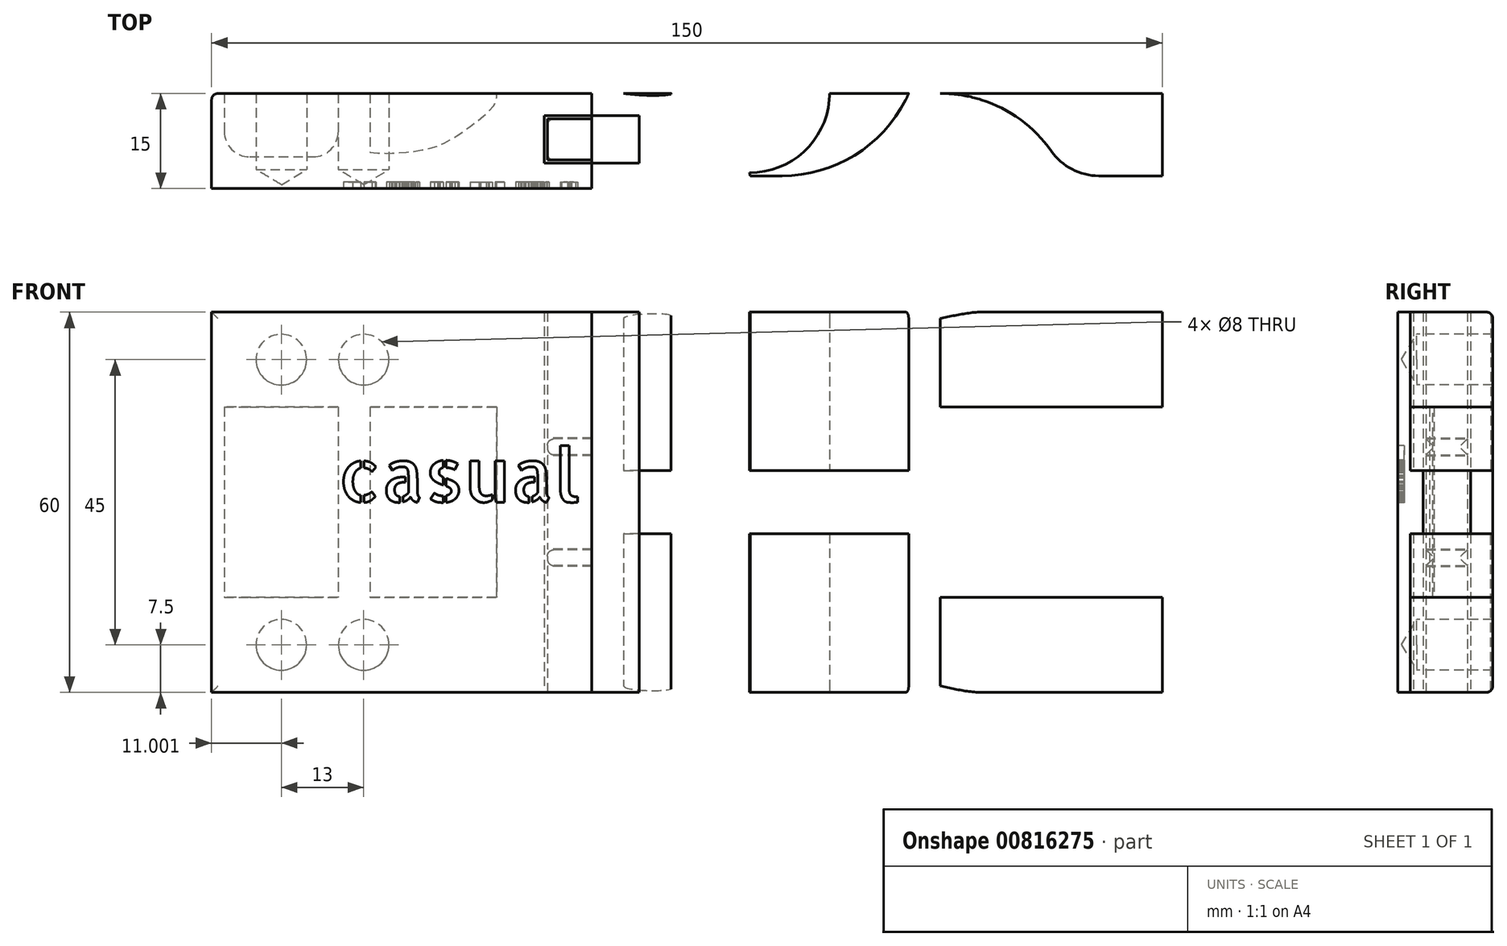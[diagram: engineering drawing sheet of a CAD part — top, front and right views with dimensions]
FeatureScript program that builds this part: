
annotation { "Feature Type Name" : "Feature", "Feature Type Description" : "" }
export const myFeature = defineFeature(function(context is Context, id is Id, definition is map)
    precondition{}
    {
        {
            var Q0;
            Q0=qCreatedBy(makeId("Top.planeOp"),FACE);
            var sketch = newSketch(context, id + "F0", { "sketchPlane" : qUnion([Q0])});
            skLineSegment(sketch, "E0.bottom", {"start": v(91.44, -7.74) * mm, "end": v(-58.56, -7.74) * mm});
            skLineSegment(sketch, "E0.top", {"start": v(91.44, 7.26) * mm, "end": v(-58.56, 7.26) * mm});
            skLineSegment(sketch, "E0.left", {"start": v(91.44, -7.74) * mm, "end": v(91.44, 7.26) * mm});
            skLineSegment(sketch, "E0.right", {"start": v(-58.56, -7.74) * mm, "end": v(-58.56, 7.26) * mm});
            skLineSegment(sketch, "E1", {"start": v(91.44, -5.74) * mm, "end": v(81.44, -5.74) * mm});
            skArc(sketch, "E2", {"start": v(81.44, -5.74) * mm, "mid": v(77.21, -4.7) * mm, "end": v(73.94, -1.84) * mm});
            skArc(sketch, "E3", {"start": v(73.94, -1.84) * mm, "mid": v(66.3, 4.85) * mm, "end": v(56.44, 7.26) * mm});
            skLineSegment(sketch, "E4", {"start": v(26.44, -5.74) * mm, "end": v(31.44, -5.74) * mm});
            skArc(sketch, "E5", {"start": v(31.44, -5.74) * mm, "mid": v(43.37, -2.2) * mm, "end": v(51.44, 7.26) * mm});
            skLineSegment(sketch, "E6", {"start": v(-58.56, -5.74) * mm, "end": v(106.76, -5.74) * mm, "construction": true});
            skFitSpline(sketch, "E7", {"points": [v(26.44, -5.74) * mm, v(25.26, -0.18) * mm, v(21.4, 5.71) * mm, v(6.44, 7.26) * mm], "startDerivative": vector(-4.01, 21.25) * mm, "endDerivative": vector(-55.89, 0) * mm});
            skLineSegment(sketch, "E8.bottom", {"start": v(-56.56, 7.26) * mm, "end": v(-38.56, 7.26) * mm});
            skLineSegment(sketch, "E8.top", {"start": v(-52.56, -2.74) * mm, "end": v(-42.56, -2.74) * mm});
            skLineSegment(sketch, "E8.left", {"start": v(-56.56, 7.26) * mm, "end": v(-56.56, 1.26) * mm});
            skLineSegment(sketch, "E8.right", {"start": v(-38.56, 7.26) * mm, "end": v(-38.56, 1.26) * mm});
            skLineSegment(sketch, "E9", {"start": v(-33.56, 7.26) * mm, "end": v(-33.56, -1.98) * mm});
            skFitSpline(sketch, "E10", {"points": [v(-33.56, -1.98) * mm, v(-29.23, -1.98) * mm, v(-23.5, -0.86) * mm, v(-18.2, 2.03) * mm, v(-13.56, 7.26) * mm], "startDerivative": vector(19.96, -2.18) * mm, "endDerivative": vector(3.98, 19.09) * mm});
            skPoint(sketch, "E11.visualSharp", {"position": v(-56.56, -2.74) * mm});
            skArc(sketch, "E11.filletArc", {"start": v(-56.56, 1.26) * mm, "mid": v(-55.39, -1.56) * mm, "end": v(-52.56, -2.74) * mm});
            skPoint(sketch, "E12.visualSharp", {"position": v(-38.56, -2.74) * mm});
            skArc(sketch, "E12.filletArc", {"start": v(-42.56, -2.74) * mm, "mid": v(-39.73, -1.56) * mm, "end": v(-38.56, 1.26) * mm});
            skCircle(sketch, "E13", {"center": v(26.44, 7.26) * mm, "radius": 12.5 * mm});
            skSolve(sketch);
        }
        {
            var Q0;
            Q0=qCreatedBy(makeId("Top.planeOp"),FACE);
            var sketch = newSketch(context, id + "F1", { "sketchPlane" : qUnion([Q0])});
            skFitSpline(sketch, "E14.0", {"points": [v(-33.56, -1.98) * mm, v(-32.12, -2.14) * mm, v(-29.23, -2.11) * mm, v(-23.2, -1.12) * mm, v(-18.34, 1.63) * mm, v(-13.92, 5.51) * mm, v(-13.56, 7.26) * mm]});
            skLineSegment(sketch, "E14.1", {"start": v(-33.56, 7.26) * mm, "end": v(-33.56, -1.98) * mm});
            skLineSegment(sketch, "E14.2", {"start": v(-38.56, 7.26) * mm, "end": v(-38.56, 1.26) * mm});
            skArc(sketch, "E14.3", {"start": v(-42.56, -2.74) * mm, "mid": v(-39.73, -1.56) * mm, "end": v(-38.56, 1.26) * mm});
            skLineSegment(sketch, "E14.4", {"start": v(-52.56, -2.74) * mm, "end": v(-42.56, -2.74) * mm});
            skArc(sketch, "E14.5", {"start": v(-56.56, 1.26) * mm, "mid": v(-55.39, -1.56) * mm, "end": v(-52.56, -2.74) * mm});
            skLineSegment(sketch, "E14.6", {"start": v(-56.56, 7.26) * mm, "end": v(-56.56, 1.26) * mm});
            skLineSegment(sketch, "E14.8", {"start": v(-58.56, -7.74) * mm, "end": v(-58.56, 7.26) * mm});
            skLineSegment(sketch, "E15", {"start": v(-58.56, -7.74) * mm, "end": v(1.44, -7.74) * mm});
            skLineSegment(sketch, "E16", {"start": v(1.44, -7.74) * mm, "end": v(1.44, 7.26) * mm});
            skLineSegment(sketch, "E17", {"start": v(1.44, 7.26) * mm, "end": v(-58.56, 7.26) * mm});
            skLineSegment(sketch, "E18.bottom", {"start": v(8.94, -3.75) * mm, "end": v(-6.06, -3.75) * mm});
            skLineSegment(sketch, "E18.top", {"start": v(8.94, 3.75) * mm, "end": v(-6.06, 3.75) * mm});
            skLineSegment(sketch, "E18.left", {"start": v(8.94, -3.75) * mm, "end": v(8.94, 3.75) * mm});
            skLineSegment(sketch, "E18.right", {"start": v(-6.06, -3.75) * mm, "end": v(-6.06, 3.75) * mm});
            skPoint(sketch, "E18.middle", {"position": v(1.44, 0) * mm});
            skFitSpline(sketch, "E19.0", {"points": [v(26.44, -5.74) * mm, v(26.08, -3.84) * mm, v(25.69, -0.2) * mm, v(21.45, 7.91) * mm, v(14.55, 7.26) * mm, v(6.44, 7.26) * mm]});
            skArc(sketch, "E19.1", {"start": v(31.44, -5.74) * mm, "mid": v(43.37, -2.2) * mm, "end": v(51.44, 7.26) * mm});
            skLineSegment(sketch, "E19.2", {"start": v(26.44, -5.74) * mm, "end": v(31.44, -5.74) * mm});
            skArc(sketch, "E19.3", {"start": v(73.94, -1.84) * mm, "mid": v(66.3, 4.85) * mm, "end": v(56.44, 7.26) * mm});
            skArc(sketch, "E19.4", {"start": v(81.44, -5.74) * mm, "mid": v(77.21, -4.7) * mm, "end": v(73.94, -1.84) * mm});
            skLineSegment(sketch, "E19.5", {"start": v(91.44, -5.74) * mm, "end": v(81.44, -5.74) * mm});
            skCircle(sketch, "E19.7", {"center": v(26.44, 7.26) * mm, "radius": 12.5 * mm});
            skLineSegment(sketch, "E20.bottom", {"start": v(1.44, 7.26) * mm, "end": v(91.44, 7.26) * mm});
            skLineSegment(sketch, "E20.top", {"start": v(1.44, -7.74) * mm, "end": v(91.44, -7.74) * mm});
            skLineSegment(sketch, "E20.left", {"start": v(1.44, 7.26) * mm, "end": v(1.44, -7.74) * mm});
            skLineSegment(sketch, "E20.right", {"start": v(91.44, 7.26) * mm, "end": v(91.44, -7.74) * mm});
            skLineSegment(sketch, "E21.0", {"start": v(8.94, 3.25) * mm, "end": v(-5.56, 3.25) * mm});
            skLineSegment(sketch, "E21.1", {"start": v(-5.56, -3.25) * mm, "end": v(-5.56, 3.25) * mm});
            skLineSegment(sketch, "E21.2", {"start": v(8.94, -3.25) * mm, "end": v(-5.56, -3.25) * mm});
            skSolve(sketch);
        }
        {
            var Q0;
            {var subQ5=sQuery(id+"F1.wireOp",EDGE,"E18.right");Q0=makeQuery(id+"F1.imprint","IMPRINT",FACE,{"disambiguationData":[TD([[makeQuery(id+"F1.imprint","IMPRINT",EDGE,{"derivedFrom":subQ5}),-1.0]])]});}
            var Q1;
            {var subQ6=sQuery(id+"F1.wireOp",EDGE,"E14.0");Q1=makeQuery(id+"F1.imprint","IMPRINT",FACE,{"disambiguationData":[TD([[makeQuery(id+"F1.imprint","IMPRINT",EDGE,{"derivedFrom":subQ6}),-1.0]])]});}
            var Q2;
            {var subQ0=sQuery(id+"F1.wireOp",EDGE,"E14.0");Q2=makeQuery(id+"F1.imprint","IMPRINT",FACE,{"disambiguationData":[TD([[makeQuery(id+"F1.imprint","IMPRINT",EDGE,{"derivedFrom":subQ0}),1.0]])]});}
            var Q3;
            {var subQ1=sQuery(id+"F1.wireOp",EDGE,"E14.2");Q3=makeQuery(id+"F1.imprint","IMPRINT",FACE,{"disambiguationData":[TD([[makeQuery(id+"F1.imprint","IMPRINT",EDGE,{"derivedFrom":subQ1}),-1.0]])]});}
            var Q4;
            {var subQ5=sQuery(id+"F1.wireOp",EDGE,"E21.1");Q4=makeQuery(id+"F1.imprint","IMPRINT",FACE,{"disambiguationData":[TD([[makeQuery(id+"F1.imprint","IMPRINT",EDGE,{"derivedFrom":subQ5}),-1.0]])]});}
            extrude(context, id + "F2", {"entities" : qUnion([Q0, Q1, Q2, Q3, Q4]), "depth" : 60 * mm, "offsetDistance" : 25 * mm, "symmetric" : true});
        }
        {
            var Q0;
            {var subQ1=sQuery(id+"F1.wireOp",EDGE,"E14.2");Q0=makeQuery(id+"F1.imprint","IMPRINT",FACE,{"disambiguationData":[TD([[makeQuery(id+"F1.imprint","IMPRINT",EDGE,{"derivedFrom":subQ1}),-1.0]])]});}
            var Q1;
            {var subQ0=sQuery(id+"F1.wireOp",EDGE,"E14.0");Q1=makeQuery(id+"F1.imprint","IMPRINT",FACE,{"disambiguationData":[TD([[makeQuery(id+"F1.imprint","IMPRINT",EDGE,{"derivedFrom":subQ0}),1.0]])]});}
            extrude(context, id + "F3", {"entities" : qUnion([Q0, Q1]), "operationType" : NewBodyOperationType.REMOVE, "depth" : 30 * mm, "offsetDistance" : 25 * mm, "symmetric" : true});
        }
        {
            var Q0;
            {var subQ5=sQuery(id+"F1.wireOp",EDGE,"E18.right");Q0=makeQuery(id+"F1.imprint","IMPRINT",FACE,{"disambiguationData":[TD([[makeQuery(id+"F1.imprint","IMPRINT",EDGE,{"derivedFrom":subQ5}),-1.0]])]});}
            var Q1;
            {var subQ5=sQuery(id+"F1.wireOp",EDGE,"E21.1");Q1=makeQuery(id+"F1.imprint","IMPRINT",FACE,{"disambiguationData":[TD([[makeQuery(id+"F1.imprint","IMPRINT",EDGE,{"derivedFrom":subQ5}),-1.0]])]});}
            extrude(context, id + "F4", {"entities" : qUnion([Q0, Q1]), "operationType" : NewBodyOperationType.REMOVE, "depth" : 20.25 * mm, "offsetDistance" : 25 * mm, "symmetric" : true});
        }
        {
            var Q0;
            {var subQ4=sQuery(id+"F1.wireOp",EDGE,"E18.left");Q0=makeQuery(id+"F1.imprint","IMPRINT",FACE,{"disambiguationData":[TD([[makeQuery(id+"F1.imprint","IMPRINT",EDGE,{"derivedFrom":subQ4}),-1.0]])]});}
            var Q1;
            {var subQ0=sQuery(id+"F1.wireOp",EDGE,"E18.left");Q1=makeQuery(id+"F1.imprint","IMPRINT",FACE,{"disambiguationData":[TD([[makeQuery(id+"F1.imprint","IMPRINT",EDGE,{"derivedFrom":subQ0}),1.0]])]});}
            extrude(context, id + "F5", {"entities" : qUnion([Q0, Q1]), "depth" : 60 * mm, "offsetDistance" : 25 * mm, "symmetric" : true});
        }
        {
            var Q0;
            {var subQ0=sQuery(id+"F1.wireOp",EDGE,"E19.7");var subQ1=sQuery(id+"F1.wireOp",EDGE,"E19.0");var subQ2=makeQuery(id+"F1.imprint","INTERSECT",VERTEX,{"disambiguationData":[OD(1.0)],"derivedFrom":[subQ1,subQ0]});Q0=makeQuery(id+"F1.imprint","IMPRINT",FACE,{"disambiguationData":[TD([[makeQuery(id+"F1.imprint","IMPRINT",EDGE,{"disambiguationData":[TD([[subQ2,-1.0]])],"derivedFrom":subQ1}),-1.0]])]});}
            var Q1;
            {var subQ0=sQuery(id+"F1.wireOp",EDGE,"E19.7");var subQ1=sQuery(id+"F1.wireOp",EDGE,"E19.0");var subQ2=makeQuery(id+"F1.imprint","INTERSECT",VERTEX,{"disambiguationData":[OD(1.0)],"derivedFrom":[subQ1,subQ0]});Q1=makeQuery(id+"F1.imprint","IMPRINT",FACE,{"disambiguationData":[TD([[makeQuery(id+"F1.imprint","IMPRINT",EDGE,{"disambiguationData":[TD([[subQ2,-1.0]])],"derivedFrom":subQ1}),1.0]])]});}
            var Q2;
            {var subQ5=sQuery(id+"F1.wireOp",EDGE,"E19.1");Q2=makeQuery(id+"F1.imprint","IMPRINT",FACE,{"disambiguationData":[TD([[makeQuery(id+"F1.imprint","IMPRINT",EDGE,{"derivedFrom":subQ5}),1.0]])]});}
            var Q3;
            {var subQ1=sQuery(id+"F1.wireOp",EDGE,"E19.3");Q3=makeQuery(id+"F1.imprint","IMPRINT",FACE,{"disambiguationData":[TD([[makeQuery(id+"F1.imprint","IMPRINT",EDGE,{"derivedFrom":subQ1}),-1.0]])]});}
            extrude(context, id + "F6", {"entities" : qUnion([Q0, Q1, Q2, Q3]), "operationType" : NewBodyOperationType.ADD, "depth" : 60 * mm, "offsetDistance" : 25 * mm, "symmetric" : true});
        }
        {
            var Q0;
            {var subQ0=sQuery(id+"F1.wireOp",EDGE,"E19.7");var subQ1=sQuery(id+"F1.wireOp",EDGE,"E19.0");var subQ2=makeQuery(id+"F1.imprint","INTERSECT",VERTEX,{"disambiguationData":[OD(0.0)],"derivedFrom":[subQ1,subQ0]});Q0=makeQuery(id+"F1.imprint","IMPRINT",FACE,{"disambiguationData":[TD([[makeQuery(id+"F1.imprint","IMPRINT",EDGE,{"disambiguationData":[TD([[subQ2,1.0]])],"derivedFrom":subQ1}),-1.0]])]});}
            extrude(context, id + "F7", {"entities" : qUnion([Q0]), "operationType" : NewBodyOperationType.ADD, "depth" : 14 * mm, "offsetDistance" : 25 * mm, "symmetric" : true});
        }
        {
            var Q0;
            {var subQ0=sQuery(id+"F1.wireOp",EDGE,"E19.7");var subQ1=sQuery(id+"F1.wireOp",EDGE,"E19.0");var subQ2=makeQuery(id+"F1.imprint","INTERSECT",VERTEX,{"disambiguationData":[OD(0.0)],"derivedFrom":[subQ1,subQ0]});Q0=makeQuery(id+"F1.imprint","IMPRINT",FACE,{"disambiguationData":[TD([[makeQuery(id+"F1.imprint","IMPRINT",EDGE,{"disambiguationData":[TD([[subQ2,1.0]])],"derivedFrom":subQ1}),-1.0]])]});}
            extrude(context, id + "F8", {"entities" : qUnion([Q0]), "operationType" : NewBodyOperationType.REMOVE, "depth" : 10 * mm, "offsetDistance" : 25 * mm, "symmetric" : true});
        }
        {
            var Q0;
            {var subQ0=sQuery(id+"F1.wireOp",EDGE,"E19.7");var subQ1=sQuery(id+"F1.wireOp",EDGE,"E19.0");var subQ2=makeQuery(id+"F1.imprint","INTERSECT",VERTEX,{"disambiguationData":[OD(1.0)],"derivedFrom":[subQ1,subQ0]});Q0=makeQuery(id+"F1.imprint","IMPRINT",FACE,{"disambiguationData":[TD([[makeQuery(id+"F1.imprint","IMPRINT",EDGE,{"disambiguationData":[TD([[subQ2,-1.0]])],"derivedFrom":subQ1}),-1.0]])]});}
            var Q1;
            {var subQ5=sQuery(id+"F1.wireOp",EDGE,"E19.1");Q1=makeQuery(id+"F1.imprint","IMPRINT",FACE,{"disambiguationData":[TD([[makeQuery(id+"F1.imprint","IMPRINT",EDGE,{"derivedFrom":subQ5}),1.0]])]});}
            extrude(context, id + "F9", {"entities" : qUnion([Q0, Q1]), "operationType" : NewBodyOperationType.REMOVE, "oppositeDirection" : true, "depth" : 10 * mm, "offsetDistance" : 25 * mm, "symmetric" : true});
        }
        {
            var Q0;
            {var subQ1=sQuery(id+"F1.wireOp",EDGE,"E19.3");Q0=makeQuery(id+"F1.imprint","IMPRINT",FACE,{"disambiguationData":[TD([[makeQuery(id+"F1.imprint","IMPRINT",EDGE,{"derivedFrom":subQ1}),-1.0]])]});}
            extrude(context, id + "F10", {"entities" : qUnion([Q0]), "operationType" : NewBodyOperationType.REMOVE, "depth" : 30 * mm, "offsetDistance" : 25 * mm, "symmetric" : true});
        }
        {
            var Q0;
            {var subQ5=sQuery(id+"F1.wireOp",EDGE,"E21.1");Q0=makeQuery(id+"F1.imprint","IMPRINT",FACE,{"disambiguationData":[TD([[makeQuery(id+"F1.imprint","IMPRINT",EDGE,{"derivedFrom":subQ5}),-1.0]])]});}
            extrude(context, id + "F11", {"entities" : qUnion([Q0]), "operationType" : NewBodyOperationType.ADD, "depth" : 20 * mm, "offsetDistance" : 25 * mm, "symmetric" : true});
        }
        {
            var Q0;
            {var subQ0=sQuery(id+"F1.wireOp",EDGE,"E20.bottom");var subQ1=makeQuery(id+"F1.imprint","INTERSECT",VERTEX,{"derivedFrom":[sQuery(id+"F1.wireOp",EDGE,"E19.3"),subQ0]});var subQ2=makeQuery(id+"F1.imprint","INTERSECT",VERTEX,{"derivedFrom":[sQuery(id+"F1.wireOp",EDGE,"E19.1"),subQ0]});var subQ3=sQuery(id+"F1.wireOp",EDGE,"E19.7");var subQ4=makeQuery(id+"F1.imprint","INTERSECT",VERTEX,{"disambiguationData":[OD(0.0)],"derivedFrom":[subQ3,subQ0]});var subQ5=sQuery(id+"F1.wireOp",EDGE,"E19.0");var subQ6=makeQuery(id+"F1.imprint","INTERSECT",VERTEX,{"disambiguationData":[OD(1.0)],"derivedFrom":[subQ5,subQ0]});var subQ8=makeQuery(id+"F1.imprint","INTERSECT",VERTEX,{"disambiguationData":[OD(0.0)],"derivedFrom":[subQ5,subQ0]});Q0=makeQuery(id+"F6.boolean.opBoolean","MERGE",EDGE,{"derivedFrom":[makeQuery(id+"F5.opExtrude","CAP_EDGE",EDGE,{"disambiguationData":[OSD([subQ0]),TDD([makeQuery(id+"F1.imprint","IMPRINT",EDGE,{"disambiguationData":[TD([[subQ8,1.0]])],"derivedFrom":subQ0}),makeQuery(id+"F1.imprint","IMPRINT",EDGE,{"disambiguationData":[TD([[subQ8,-1.0]])],"derivedFrom":subQ0})])],"isStart":false}),makeQuery(id+"F5.opExtrude","CAP_EDGE",EDGE,{"disambiguationData":[OSD([subQ0]),TDD([makeQuery(id+"F1.imprint","IMPRINT",EDGE,{"disambiguationData":[TD([[subQ2,-1.0]])],"derivedFrom":subQ0})])],"isStart":false}),makeQuery(id+"F6.opExtrude","CAP_EDGE",EDGE,{"disambiguationData":[OSD([subQ0]),TDD([makeQuery(id+"F1.imprint","IMPRINT",EDGE,{"disambiguationData":[TD([[subQ6,1.0]])],"derivedFrom":subQ0}),makeQuery(id+"F1.imprint","IMPRINT",EDGE,{"disambiguationData":[TD([[subQ4,1.0]])],"derivedFrom":subQ0}),makeQuery(id+"F1.imprint","IMPRINT",EDGE,{"disambiguationData":[TD([[subQ2,1.0]])],"derivedFrom":subQ0})])],"isStart":false}),makeQuery(id+"F6.opExtrude","CAP_EDGE",EDGE,{"disambiguationData":[OSD([subQ0]),TDD([makeQuery(id+"F1.imprint","IMPRINT",EDGE,{"disambiguationData":[TD([[subQ1,-1.0]])],"derivedFrom":subQ0})])],"isStart":false})]});}
            var Q1;
            {var subQ0=sQuery(id+"F1.wireOp",EDGE,"E20.bottom");var subQ3=sQuery(id+"F1.wireOp",EDGE,"E20.right");var subQ4=sQuery(id+"F1.wireOp",EDGE,"E19.1");var subQ6=sQuery(id+"F1.wireOp",EDGE,"E19.7");var subQ8=sQuery(id+"F1.wireOp",EDGE,"E19.0");var subQ13=sQuery(id+"F1.wireOp",EDGE,"E19.2");Q1=makeQuery(id+"F10.boolean.opBoolean","SPLIT",EDGE,{"disambiguationData":[TD([makeQuery(id+"F6.opExtrude","CAP_FACE",FACE,{"disambiguationData":[OSD([subQ8,subQ4,subQ13,subQ6,subQ0])],"isStart":false})])],"derivedFrom":makeQuery(id+"F6.opExtrude","SWEPT_EDGE",EDGE,{"disambiguationData":[OSD([subQ0,subQ3])]})});}
            var Q2;
            {var subQ0=sQuery(id+"F1.wireOp",EDGE,"E20.right");var subQ1=sQuery(id+"F1.wireOp",EDGE,"E20.bottom");var subQ2=sQuery(id+"F1.wireOp",EDGE,"E19.1");var subQ4=sQuery(id+"F1.wireOp",EDGE,"E19.7");var subQ6=sQuery(id+"F1.wireOp",EDGE,"E19.0");var subQ11=sQuery(id+"F1.wireOp",EDGE,"E19.2");Q2=makeQuery(id+"F10.boolean.opBoolean","SPLIT",EDGE,{"disambiguationData":[TD([makeQuery(id+"F6.opExtrude","CAP_FACE",FACE,{"disambiguationData":[OSD([subQ6,subQ2,subQ11,subQ4,subQ1])],"isStart":true})])],"derivedFrom":makeQuery(id+"F6.opExtrude","SWEPT_EDGE",EDGE,{"disambiguationData":[OSD([subQ1,subQ0])]})});}
            var Q3;
            {var subQ0=sQuery(id+"F1.wireOp",EDGE,"E20.bottom");var subQ1=makeQuery(id+"F1.imprint","INTERSECT",VERTEX,{"derivedFrom":[sQuery(id+"F1.wireOp",EDGE,"E19.3"),subQ0]});var subQ2=makeQuery(id+"F1.imprint","INTERSECT",VERTEX,{"derivedFrom":[sQuery(id+"F1.wireOp",EDGE,"E19.1"),subQ0]});var subQ3=sQuery(id+"F1.wireOp",EDGE,"E19.7");var subQ4=makeQuery(id+"F1.imprint","INTERSECT",VERTEX,{"disambiguationData":[OD(0.0)],"derivedFrom":[subQ3,subQ0]});var subQ5=sQuery(id+"F1.wireOp",EDGE,"E19.0");var subQ6=makeQuery(id+"F1.imprint","INTERSECT",VERTEX,{"disambiguationData":[OD(1.0)],"derivedFrom":[subQ5,subQ0]});var subQ8=makeQuery(id+"F1.imprint","INTERSECT",VERTEX,{"disambiguationData":[OD(0.0)],"derivedFrom":[subQ5,subQ0]});Q3=makeQuery(id+"F6.boolean.opBoolean","MERGE",EDGE,{"derivedFrom":[makeQuery(id+"F5.opExtrude","CAP_EDGE",EDGE,{"disambiguationData":[OSD([subQ0]),TDD([makeQuery(id+"F1.imprint","IMPRINT",EDGE,{"disambiguationData":[TD([[subQ8,1.0]])],"derivedFrom":subQ0}),makeQuery(id+"F1.imprint","IMPRINT",EDGE,{"disambiguationData":[TD([[subQ8,-1.0]])],"derivedFrom":subQ0})])],"isStart":true}),makeQuery(id+"F5.opExtrude","CAP_EDGE",EDGE,{"disambiguationData":[OSD([subQ0]),TDD([makeQuery(id+"F1.imprint","IMPRINT",EDGE,{"disambiguationData":[TD([[subQ2,-1.0]])],"derivedFrom":subQ0})])],"isStart":true}),makeQuery(id+"F6.opExtrude","CAP_EDGE",EDGE,{"disambiguationData":[OSD([subQ0]),TDD([makeQuery(id+"F1.imprint","IMPRINT",EDGE,{"disambiguationData":[TD([[subQ6,1.0]])],"derivedFrom":subQ0}),makeQuery(id+"F1.imprint","IMPRINT",EDGE,{"disambiguationData":[TD([[subQ4,1.0]])],"derivedFrom":subQ0}),makeQuery(id+"F1.imprint","IMPRINT",EDGE,{"disambiguationData":[TD([[subQ2,1.0]])],"derivedFrom":subQ0})])],"isStart":true}),makeQuery(id+"F6.opExtrude","CAP_EDGE",EDGE,{"disambiguationData":[OSD([subQ0]),TDD([makeQuery(id+"F1.imprint","IMPRINT",EDGE,{"disambiguationData":[TD([[subQ1,-1.0]])],"derivedFrom":subQ0})])],"isStart":true})]});}
            var Q4;
            Q4=makeQuery(id+"F2.opExtrude","CAP_EDGE",EDGE,{"disambiguationData":[OSD([sQuery(id+"F1.wireOp",EDGE,"E17")])],"isStart":false});
            var Q5;
            Q5=makeQuery(id+"F2.opExtrude","SWEPT_EDGE",EDGE,{"disambiguationData":[OSD([sQuery(id+"F1.wireOp",EDGE,"E14.8"),sQuery(id+"F1.wireOp",EDGE,"E17")])]});
            var Q6;
            Q6=makeQuery(id+"F2.opExtrude","CAP_EDGE",EDGE,{"disambiguationData":[OSD([sQuery(id+"F1.wireOp",EDGE,"E17")])],"isStart":true});
            var Q7;
            Q7=makeQuery(id+"F3.boolean.opBoolean","COPY",EDGE,{"derivedFrom":makeQuery(id+"F3.opExtrude","SWEPT_EDGE",EDGE,{"disambiguationData":[OSD([sQuery(id+"F1.wireOp",EDGE,"E14.6"),sQuery(id+"F1.wireOp",EDGE,"E17")])]})});
            var Q8;
            Q8=makeQuery(id+"F3.boolean.opBoolean","COPY",EDGE,{"derivedFrom":makeQuery(id+"F3.opExtrude","SWEPT_EDGE",EDGE,{"disambiguationData":[OSD([sQuery(id+"F1.wireOp",EDGE,"E14.2"),sQuery(id+"F1.wireOp",EDGE,"E17")])]})});
            var Q9;
            Q9=makeQuery(id+"F3.boolean.opBoolean","COPY",EDGE,{"derivedFrom":makeQuery(id+"F3.opExtrude","SWEPT_EDGE",EDGE,{"disambiguationData":[OSD([sQuery(id+"F1.wireOp",EDGE,"E14.1"),sQuery(id+"F1.wireOp",EDGE,"E17")])]})});
            var Q10;
            {var subQ0=sQuery(id+"F1.wireOp",EDGE,"E17");Q10=makeQuery(id+"F3.boolean.opBoolean","COPY",EDGE,{"derivedFrom":makeQuery(id+"F3.opExtrude","CAP_EDGE",EDGE,{"disambiguationData":[OSD([subQ0]),TDD([makeQuery(id+"F1.imprint","IMPRINT",EDGE,{"disambiguationData":[TD([[makeQuery(id+"F1.imprint","INTERSECT",VERTEX,{"derivedFrom":[sQuery(id+"F1.wireOp",EDGE,"E14.2"),subQ0]}),-1.0]])],"derivedFrom":subQ0})])],"isStart":true})});}
            var Q11;
            {var subQ0=sQuery(id+"F1.wireOp",EDGE,"E17");Q11=makeQuery(id+"F3.boolean.opBoolean","COPY",EDGE,{"derivedFrom":makeQuery(id+"F3.opExtrude","CAP_EDGE",EDGE,{"disambiguationData":[OSD([subQ0]),TDD([makeQuery(id+"F1.imprint","IMPRINT",EDGE,{"disambiguationData":[TD([[makeQuery(id+"F1.imprint","INTERSECT",VERTEX,{"derivedFrom":[sQuery(id+"F1.wireOp",EDGE,"E14.2"),subQ0]}),-1.0]])],"derivedFrom":subQ0})])],"isStart":false})});}
            fillet(context, id + "F12", {"entities" : qUnion([Q0, Q1, Q2, Q3, Q4, Q5, Q6, Q7, Q8, Q9, Q10, Q11]), "radius" : 1 * mm, "tangentPropagation" : true, "allowEdgeOverflow" : false});
        }
        {
            var Q0;
            {var subQ5=sQuery(id+"F1.wireOp",EDGE,"E21.1");Q0=makeQuery(id+"F1.imprint","IMPRINT",FACE,{"disambiguationData":[TD([[makeQuery(id+"F1.imprint","IMPRINT",EDGE,{"derivedFrom":subQ5}),-1.0]])]});}
            extrude(context, id + "F13", {"entities" : qUnion([Q0]), "operationType" : NewBodyOperationType.REMOVE, "depth" : 15 * mm, "offsetDistance" : 25 * mm, "symmetric" : true});
        }
        {
            var Q0;
            {var subQ0=sQuery(id+"F1.wireOp",EDGE,"E21.2");var subQ1=sQuery(id+"F1.wireOp",EDGE,"E21.1");var subQ2=sQuery(id+"F1.wireOp",EDGE,"E21.0");var subQ3=sQuery(id+"F1.wireOp",EDGE,"E20.left");Q0=makeQuery(id+"F13.boolean.opBoolean","SPLIT",FACE,{"disambiguationData":[TD([makeQuery(id+"F11.opExtrude","CAP_FACE",FACE,{"disambiguationData":[OSD([subQ3,subQ2,subQ1,subQ0])],"isStart":true})])],"derivedFrom":makeQuery(id+"F11.opExtrude","SWEPT_FACE",FACE,{"disambiguationData":[OSD([subQ1])]})});}
            var Q1;
            {var subQ0=sQuery(id+"F1.wireOp",EDGE,"E21.2");var subQ1=sQuery(id+"F1.wireOp",EDGE,"E21.1");var subQ2=sQuery(id+"F1.wireOp",EDGE,"E21.0");var subQ3=sQuery(id+"F1.wireOp",EDGE,"E20.left");Q1=makeQuery(id+"F13.boolean.opBoolean","SPLIT",FACE,{"disambiguationData":[TD([makeQuery(id+"F11.opExtrude","CAP_FACE",FACE,{"disambiguationData":[OSD([subQ3,subQ2,subQ1,subQ0])],"isStart":false})])],"derivedFrom":makeQuery(id+"F11.opExtrude","SWEPT_FACE",FACE,{"disambiguationData":[OSD([subQ1])]})});}
            fillet(context, id + "F14", {"entities" : qUnion([Q0, Q1]), "radius" : 1 * mm, "tangentPropagation" : true, "allowEdgeOverflow" : false});
        }
        {
            var Q0;
            {var subQ5=sQuery(id+"F1.wireOp",EDGE,"E21.1");Q0=makeQuery(id+"F1.imprint","IMPRINT",FACE,{"disambiguationData":[TD([[makeQuery(id+"F1.imprint","IMPRINT",EDGE,{"derivedFrom":subQ5}),-1.0]])]});}
            var Q1;
            {var subQ5=sQuery(id+"F1.wireOp",EDGE,"E18.right");Q1=makeQuery(id+"F1.imprint","IMPRINT",FACE,{"disambiguationData":[TD([[makeQuery(id+"F1.imprint","IMPRINT",EDGE,{"derivedFrom":subQ5}),-1.0]])]});}
            extrude(context, id + "F15", {"entities" : qUnion([Q0, Q1]), "operationType" : NewBodyOperationType.ADD, "depth" : 14.75 * mm, "offsetDistance" : 25 * mm, "symmetric" : true});
        }
        {
            var Q0;
            Q0=makeQuery(id+"F2.opExtrude","SWEPT_FACE",FACE,{"disambiguationData":[OSD([sQuery(id+"F1.wireOp",EDGE,"E15")])]});
            var sketch = newSketch(context, id + "F16", { "sketchPlane" : qUnion([Q0])});
            skText(sketch, "E22", { "text": "casual", "fontName": "AllertaStencil-Regular.ttf"});
            skText(sketch, "E23", { "text": "Tanker", "fontName": "AllertaStencil-Regular.ttf"});
            const initialGuessF16  = {"E22": [-0.03855, 0, 1, 0, 0.0085], "E23": [0.00288, -0.0085, 1, 0, 0.0085]};
            skSetInitialGuess(sketch, initialGuessF16);
            skSolve(sketch);
        }
        {
            var Q0;
            Q0=makeQuery(id+"F16.imprint","IMPRINT",FACE,{"disambiguationData":[TD([[makeQuery(id+"F16.imprint","IMPRINT",EDGE,{"derivedFrom":sQuery(id+"F16.wireOp",EDGE,"E22.sketch_text.stroke-11")}),-1.0]])]});
            var Q1;
            Q1=makeQuery(id+"F16.imprint","IMPRINT",FACE,{"disambiguationData":[TD([[makeQuery(id+"F16.imprint","IMPRINT",EDGE,{"derivedFrom":sQuery(id+"F16.wireOp",EDGE,"E22.sketch_text.stroke-0")}),-1.0]])]});
            var Q2;
            Q2=makeQuery(id+"F16.imprint","IMPRINT",FACE,{"disambiguationData":[TD([[makeQuery(id+"F16.imprint","IMPRINT",EDGE,{"derivedFrom":sQuery(id+"F16.wireOp",EDGE,"E22.sketch_text.stroke-5")}),-1.0]])]});
            var Q3;
            Q3=makeQuery(id+"F16.imprint","IMPRINT",FACE,{"disambiguationData":[TD([[makeQuery(id+"F16.imprint","IMPRINT",EDGE,{"derivedFrom":sQuery(id+"F16.wireOp",EDGE,"E22.sketch_text.stroke-29")}),-1.0]])]});
            var Q4;
            Q4=makeQuery(id+"F16.imprint","IMPRINT",FACE,{"disambiguationData":[TD([[makeQuery(id+"F16.imprint","IMPRINT",EDGE,{"derivedFrom":sQuery(id+"F16.wireOp",EDGE,"E22.sketch_text.stroke-48")}),-1.0]])]});
            var Q5;
            Q5=makeQuery(id+"F16.imprint","IMPRINT",FACE,{"disambiguationData":[TD([[makeQuery(id+"F16.imprint","IMPRINT",EDGE,{"derivedFrom":sQuery(id+"F16.wireOp",EDGE,"E22.sketch_text.stroke-84")}),-1.0]])]});
            var Q6;
            Q6=makeQuery(id+"F16.imprint","IMPRINT",FACE,{"disambiguationData":[TD([[makeQuery(id+"F16.imprint","IMPRINT",EDGE,{"derivedFrom":sQuery(id+"F16.wireOp",EDGE,"E22.sketch_text.stroke-98")}),-1.0]])]});
            var Q7;
            Q7=makeQuery(id+"F16.imprint","IMPRINT",FACE,{"disambiguationData":[TD([[makeQuery(id+"F16.imprint","IMPRINT",EDGE,{"derivedFrom":sQuery(id+"F16.wireOp",EDGE,"E22.sketch_text.stroke-113")}),-1.0]])]});
            var Q8;
            Q8=makeQuery(id+"F16.imprint","IMPRINT",FACE,{"disambiguationData":[TD([[makeQuery(id+"F16.imprint","IMPRINT",EDGE,{"derivedFrom":sQuery(id+"F16.wireOp",EDGE,"E22.sketch_text.stroke-104")}),-1.0]])]});
            var Q9;
            Q9=makeQuery(id+"F16.imprint","IMPRINT",FACE,{"disambiguationData":[TD([[makeQuery(id+"F16.imprint","IMPRINT",EDGE,{"derivedFrom":sQuery(id+"F16.wireOp",EDGE,"E22.sketch_text.stroke-127")}),-1.0]])]});
            var Q10;
            Q10=makeQuery(id+"F16.imprint","IMPRINT",FACE,{"disambiguationData":[TD([[makeQuery(id+"F16.imprint","IMPRINT",EDGE,{"derivedFrom":sQuery(id+"F16.wireOp",EDGE,"E22.sketch_text.stroke-147")}),-1.0]])]});
            var Q11;
            Q11=makeQuery(id+"F16.imprint","IMPRINT",FACE,{"disambiguationData":[TD([[makeQuery(id+"F16.imprint","IMPRINT",EDGE,{"derivedFrom":sQuery(id+"F16.wireOp",EDGE,"E22.sketch_text.stroke-152")}),-1.0]])]});
            var Q12;
            Q12=makeQuery(id+"F16.imprint","IMPRINT",FACE,{"disambiguationData":[TD([[makeQuery(id+"F16.imprint","IMPRINT",EDGE,{"derivedFrom":sQuery(id+"F16.wireOp",EDGE,"E22.sketch_text.stroke-171")}),-1.0]])]});
            var Q13;
            Q13=makeQuery(id+"F16.imprint","IMPRINT",FACE,{"disambiguationData":[TD([[makeQuery(id+"F16.imprint","IMPRINT",EDGE,{"derivedFrom":sQuery(id+"F16.wireOp",EDGE,"E22.sketch_text.stroke-207")}),-1.0]])]});
            var Q14;
            Q14=makeQuery(id+"F16.imprint","IMPRINT",FACE,{"disambiguationData":[TD([[makeQuery(id+"F16.imprint","IMPRINT",EDGE,{"derivedFrom":sQuery(id+"F16.wireOp",EDGE,"E22.sketch_text.stroke-12")}),-1.0]])]});
            extrude(context, id + "F17", {"entities" : qUnion([Q0, Q1, Q2, Q3, Q4, Q5, Q6, Q7, Q8, Q9, Q10, Q11, Q12, Q13, Q14]), "operationType" : NewBodyOperationType.REMOVE, "oppositeDirection" : true, "depth" : 1 * mm, "offsetDistance" : 25 * mm});
        }
        {
            var Q0;
            Q0=makeQuery(id+"F16.imprint","IMPRINT",FACE,{"disambiguationData":[TD([[makeQuery(id+"F16.imprint","IMPRINT",EDGE,{"derivedFrom":sQuery(id+"F16.wireOp",EDGE,"E23.sketch_text.stroke-0")}),-1.0]])]});
            var Q1;
            Q1=makeQuery(id+"F16.imprint","IMPRINT",FACE,{"disambiguationData":[TD([[makeQuery(id+"F16.imprint","IMPRINT",EDGE,{"derivedFrom":sQuery(id+"F16.wireOp",EDGE,"E23.sketch_text.stroke-8")}),-1.0]])]});
            var Q2;
            Q2=makeQuery(id+"F16.imprint","IMPRINT",FACE,{"disambiguationData":[TD([[makeQuery(id+"F16.imprint","IMPRINT",EDGE,{"derivedFrom":sQuery(id+"F16.wireOp",EDGE,"E23.sketch_text.stroke-27")}),-1.0]])]});
            var Q3;
            Q3=makeQuery(id+"F16.imprint","IMPRINT",FACE,{"disambiguationData":[TD([[makeQuery(id+"F16.imprint","IMPRINT",EDGE,{"derivedFrom":sQuery(id+"F16.wireOp",EDGE,"E23.sketch_text.stroke-63")}),-1.0]])]});
            var Q4;
            Q4=makeQuery(id+"F16.imprint","IMPRINT",FACE,{"disambiguationData":[TD([[makeQuery(id+"F16.imprint","IMPRINT",EDGE,{"derivedFrom":sQuery(id+"F16.wireOp",EDGE,"E23.sketch_text.stroke-68")}),-1.0]])]});
            var Q5;
            Q5=makeQuery(id+"F16.imprint","IMPRINT",FACE,{"disambiguationData":[TD([[makeQuery(id+"F16.imprint","IMPRINT",EDGE,{"derivedFrom":sQuery(id+"F16.wireOp",EDGE,"E23.sketch_text.stroke-94")}),-1.0]])]});
            var Q6;
            Q6=makeQuery(id+"F16.imprint","IMPRINT",FACE,{"disambiguationData":[TD([[makeQuery(id+"F16.imprint","IMPRINT",EDGE,{"derivedFrom":sQuery(id+"F16.wireOp",EDGE,"E23.sketch_text.stroke-87")}),-1.0]])]});
            var Q7;
            Q7=makeQuery(id+"F16.imprint","IMPRINT",FACE,{"disambiguationData":[TD([[makeQuery(id+"F16.imprint","IMPRINT",EDGE,{"derivedFrom":sQuery(id+"F16.wireOp",EDGE,"E23.sketch_text.stroke-111")}),-1.0]])]});
            var Q8;
            Q8=makeQuery(id+"F16.imprint","IMPRINT",FACE,{"disambiguationData":[TD([[makeQuery(id+"F16.imprint","IMPRINT",EDGE,{"derivedFrom":sQuery(id+"F16.wireOp",EDGE,"E23.sketch_text.stroke-98")}),-1.0]])]});
            var Q9;
            Q9=makeQuery(id+"F16.imprint","IMPRINT",FACE,{"disambiguationData":[TD([[makeQuery(id+"F16.imprint","IMPRINT",EDGE,{"derivedFrom":sQuery(id+"F16.wireOp",EDGE,"E23.sketch_text.stroke-135")}),-1.0]])]});
            var Q10;
            Q10=makeQuery(id+"F16.imprint","IMPRINT",FACE,{"disambiguationData":[TD([[makeQuery(id+"F16.imprint","IMPRINT",EDGE,{"derivedFrom":sQuery(id+"F16.wireOp",EDGE,"E23.sketch_text.stroke-142")}),-1.0]])]});
            extrude(context, id + "F18", {"entities" : qUnion([Q0, Q1, Q2, Q3, Q4, Q5, Q6, Q7, Q8, Q9, Q10]), "operationType" : NewBodyOperationType.REMOVE, "oppositeDirection" : true, "depth" : 1 * mm, "offsetDistance" : 25 * mm});
        }
        {
            var Q0;
            Q0=makeQuery(id+"F2.opExtrude","SWEPT_FACE",FACE,{"disambiguationData":[OSD([sQuery(id+"F1.wireOp",EDGE,"E17")])]});
            var sketch = newSketch(context, id + "F19", { "sketchPlane" : qUnion([Q0])});
            skPoint(sketch, "E24", {"position": v(47.56, 22.5) * mm});
            skPoint(sketch, "E24.positionSnap0", {"position": v(57.56, 22.5) * mm});
            skPoint(sketch, "E25", {"position": v(34.56, 22.5) * mm});
            skPoint(sketch, "E26.MirrorP", {"position": v(47.56, -22.5) * mm});
            skPoint(sketch, "E27.MirrorP", {"position": v(34.56, -22.5) * mm});
            skPoint(sketch, "E28", {"position": v(47.56, 16) * mm});
            skSolve(sketch);
        }
        {
            var Q0;
            Q0=sQuery(id+"F19.wireOp",VERTEX,"E24");
            var Q1;
            Q1=sQuery(id+"F19.wireOp",VERTEX,"E25");
            var Q2;
            Q2=sQuery(id+"F19.wireOp",VERTEX,"E26.MirrorP");
            var Q3;
            Q3=sQuery(id+"F19.wireOp",VERTEX,"E27.MirrorP");
            var Q4;
            Q4=makeQuery(id+"F2.opExtrude","SWEPT_BODY",BODY,{"disambiguationData":[OSD([sQuery(id+"F1.wireOp",EDGE,"E14.8"),sQuery(id+"F1.wireOp",EDGE,"E15"),sQuery(id+"F1.wireOp",EDGE,"E17"),sQuery(id+"F1.wireOp",EDGE,"E20.left")])]});
            hole(context, id + "F20", {"style" : HoleStyle.SIMPLE, "endStyle" : HoleEndStyle.BLIND, "holeDiameter" : 8 * mm, "majorDiameter" : 5 * mm, "holeDepth" : 12 * mm, "isTappedThrough" : true, "tappedDepth" : 12 * mm, "tapClearance" : 3, "locations" : qUnion([Q0, Q1, Q2, Q3]), "scope" : qUnion([Q4]), "startStyle" : HoleStartStyle.PART});
        }
    });
